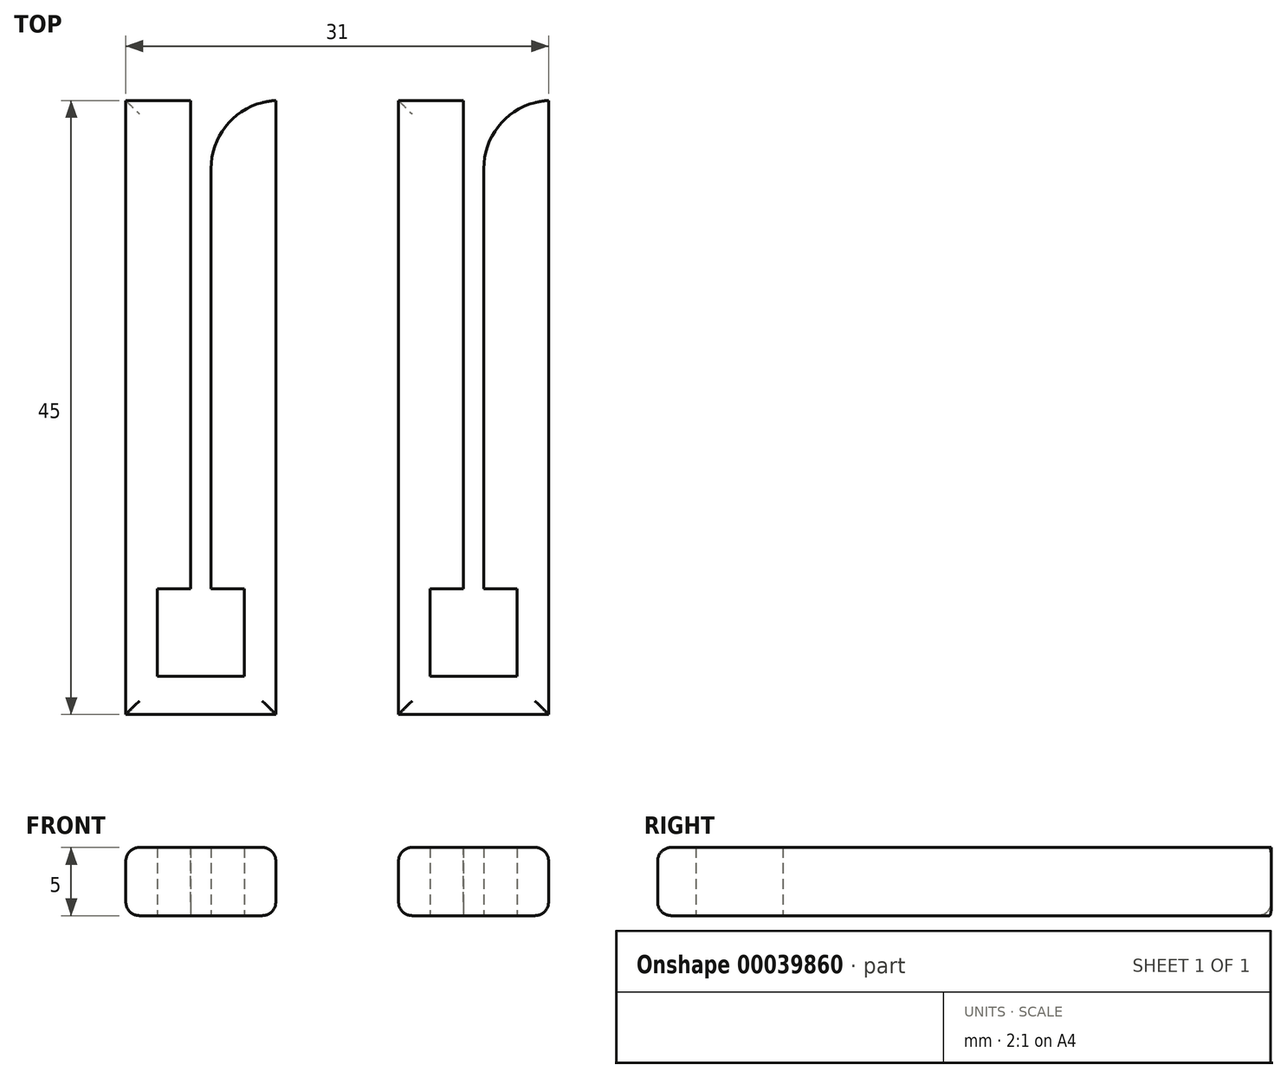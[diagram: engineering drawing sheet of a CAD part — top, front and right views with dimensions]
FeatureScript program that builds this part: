
annotation { "Feature Type Name" : "Feature", "Feature Type Description" : "" }
export const myFeature = defineFeature(function(context is Context, id is Id, definition is map)
    precondition{}
    {
        {
            var Q0;
            Q0=qCreatedBy(makeId("Top.planeOp"),FACE);
            var sketch = newSketch(context, id + "F0", { "sketchPlane" : qUnion([Q0])});
            skLineSegment(sketch, "E0.rect.bottom", {"start": v(-5.5, 22.5) * mm, "end": v(5.5, 22.5) * mm});
            skLineSegment(sketch, "E0.rect.top", {"start": v(-5.5, -22.5) * mm, "end": v(5.5, -22.5) * mm});
            skLineSegment(sketch, "E0.rect.left", {"start": v(-5.5, 22.5) * mm, "end": v(-5.5, -22.5) * mm});
            skLineSegment(sketch, "E0.rect.right", {"start": v(5.5, 22.5) * mm, "end": v(5.5, -22.5) * mm});
            skPoint(sketch, "E0.rect.middle", {"position": v(0, 0) * mm});
            skLineSegment(sketch, "E1", {"start": v(0, -22.5) * mm, "end": v(0, -16.5) * mm, "construction": true});
            skPoint(sketch, "E1.endSnap0", {"position": v(0, -22.5) * mm});
            skLineSegment(sketch, "E2.rect.bottom", {"start": v(3.2, -19.7) * mm, "end": v(-3.2, -19.7) * mm});
            skLineSegment(sketch, "E2.rect.top", {"start": v(3.2, -13.3) * mm, "end": v(-3.2, -13.3) * mm});
            skLineSegment(sketch, "E2.rect.left", {"start": v(3.2, -19.7) * mm, "end": v(3.2, -13.3) * mm});
            skLineSegment(sketch, "E2.rect.right", {"start": v(-3.2, -19.7) * mm, "end": v(-3.2, -13.3) * mm});
            skPoint(sketch, "E2.rect.middle", {"position": v(0, -16.5) * mm});
            skPoint(sketch, "E2.rect.cornerSnap0", {"position": v(-0.9, -19.7) * mm});
            skSolve(sketch);
        }
        {
            var Q0;
            Q0=qSketchRegion(id+"F0",true);
            extrude(context, id + "F1", {"entities" : qUnion([Q0]), "depth" : 5 * mm});
        }
        {
            var Q0;
            Q0=makeQuery(id+"F1.opExtrude","SWEPT_FACE",FACE,{"disambiguationData":[OSD([sQuery(id+"F0.wireOp",EDGE,"E0.rect.bottom")])]});
            var sketch = newSketch(context, id + "F2", { "sketchPlane" : qUnion([Q0])});
            skLineSegment(sketch, "E3.rect.bottom", {"start": v(-0.75, 0) * mm, "end": v(0.75, 0) * mm});
            skLineSegment(sketch, "E3.rect.top", {"start": v(-0.75, 10) * mm, "end": v(0.75, 10) * mm});
            skLineSegment(sketch, "E3.rect.left", {"start": v(-0.75, 0) * mm, "end": v(-0.75, 10) * mm});
            skLineSegment(sketch, "E3.rect.right", {"start": v(0.75, 0) * mm, "end": v(0.75, 10) * mm});
            skPoint(sketch, "E3.rect.middle", {"position": v(0, 5) * mm});
            skSolve(sketch);
        }
        {
            var Q0;
            Q0=qSketchRegion(id+"F2",true);
            extrude(context, id + "F3", {"entities" : qUnion([Q0]), "operationType" : NewBodyOperationType.REMOVE, "oppositeDirection" : true, "depth" : 37 * mm});
        }
        {
            var Q0;
            Q0=makeQuery(id+"F3.boolean.opBoolean","COPY",EDGE,{"derivedFrom":makeQuery(id+"F3.opExtrude","CAP_EDGE",EDGE,{"disambiguationData":[OSD([sQuery(id+"F2.wireOp",EDGE,"E3.rect.right")])],"isStart":true})});
            var Q1;
            Q1=makeQuery(id+"F3.boolean.opBoolean","COPY",EDGE,{"derivedFrom":makeQuery(id+"F3.opExtrude","CAP_EDGE",EDGE,{"disambiguationData":[OSD([sQuery(id+"F2.wireOp",EDGE,"E3.rect.left")])],"isStart":true})});
            fillet(context, id + "F4", {"entities" : qUnion([Q0, Q1]), "radius" : 5 * mm, "tangentPropagation" : true, "allowEdgeOverflow" : false});
        }
        {
            var Q0;
            Q0=makeQuery(id+"F3.boolean.opBoolean","COPY",EDGE,{"derivedFrom":makeQuery(id+"F3.opExtrude","CAP_EDGE",EDGE,{"disambiguationData":[OSD([sQuery(id+"F2.wireOp",EDGE,"E3.rect.bottom")])],"isStart":true})});
            var Q1;
            Q1=makeQuery(id+"F1.opExtrude","CAP_EDGE",EDGE,{"disambiguationData":[OSD([sQuery(id+"F0.wireOp",EDGE,"E0.rect.left")])],"isStart":false});
            var Q2;
            Q2=makeQuery(id+"F1.opExtrude","CAP_EDGE",EDGE,{"disambiguationData":[OSD([sQuery(id+"F0.wireOp",EDGE,"E0.rect.right")])],"isStart":false});
            var Q3;
            Q3=makeQuery(id+"F1.opExtrude","CAP_EDGE",EDGE,{"disambiguationData":[OSD([sQuery(id+"F0.wireOp",EDGE,"E0.rect.bottom")])],"isStart":true});
            var Q4;
            Q4=makeQuery(id+"F1.opExtrude","CAP_EDGE",EDGE,{"disambiguationData":[OSD([sQuery(id+"F0.wireOp",EDGE,"E0.rect.right")])],"isStart":true});
            var Q5;
            Q5=makeQuery(id+"F1.opExtrude","CAP_EDGE",EDGE,{"disambiguationData":[OSD([sQuery(id+"F0.wireOp",EDGE,"E0.rect.left")])],"isStart":true});
            var Q6;
            Q6=makeQuery(id+"F1.opExtrude","CAP_EDGE",EDGE,{"disambiguationData":[OSD([sQuery(id+"F0.wireOp",EDGE,"E0.rect.top")])],"isStart":false});
            var Q7;
            Q7=makeQuery(id+"F1.opExtrude","CAP_EDGE",EDGE,{"disambiguationData":[OSD([sQuery(id+"F0.wireOp",EDGE,"E0.rect.top")])],"isStart":true});
            fillet(context, id + "F5", {"entities" : qUnion([Q0, Q1, Q2, Q3, Q4, Q5, Q6, Q7]), "radius" : 1 * mm, "tangentPropagation" : true, "allowEdgeOverflow" : false});
        }
        {
            var Q0;
            Q0=makeQuery(id+"F1.opExtrude","SWEPT_BODY",BODY,{"disambiguationData":[OSD([sQuery(id+"F0.wireOp",EDGE,"E0.rect.bottom"),sQuery(id+"F0.wireOp",EDGE,"E0.rect.top"),sQuery(id+"F0.wireOp",EDGE,"E0.rect.left"),sQuery(id+"F0.wireOp",EDGE,"E0.rect.right"),sQuery(id+"F0.wireOp",EDGE,"E2.rect.bottom"),sQuery(id+"F0.wireOp",EDGE,"E2.rect.top"),sQuery(id+"F0.wireOp",EDGE,"E2.rect.left"),sQuery(id+"F0.wireOp",EDGE,"E2.rect.right")])]});
            transform(context, id + "F6", {"entities" : qUnion([Q0]), "transformType" : TransformType.TRANSLATION_3D, "dx" : 20 * mm, "dy" : 0 * mm, "dz" : 0 * mm, "makeCopy" : true});
        }
    });
